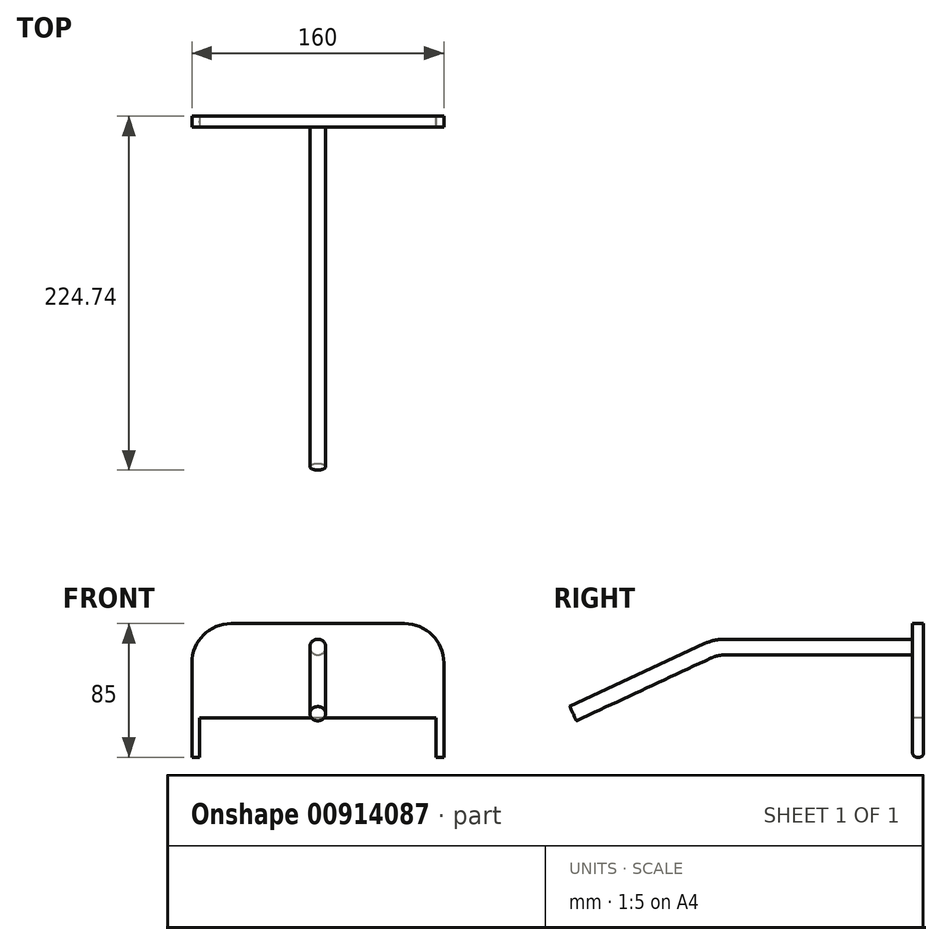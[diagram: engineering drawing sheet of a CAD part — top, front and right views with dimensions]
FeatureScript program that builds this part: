
annotation { "Feature Type Name" : "Feature", "Feature Type Description" : "" }
export const myFeature = defineFeature(function(context is Context, id is Id, definition is map)
    precondition{}
    {
        {
            var Q0;
            Q0=qCreatedBy(makeId("Right.planeOp"),FACE);
            var sketch = newSketch(context, id + "F0", { "sketchPlane" : qUnion([Q0])});
            skLineSegment(sketch, "E0.bottom", {"start": v(3.5, 30) * mm, "end": v(-3.5, 30) * mm});
            skLineSegment(sketch, "E0.top", {"start": v(3.5, -30) * mm, "end": v(-3.5, -30) * mm});
            skLineSegment(sketch, "E0.left", {"start": v(3.5, 30) * mm, "end": v(3.5, -30) * mm});
            skLineSegment(sketch, "E0.right", {"start": v(-3.5, 30) * mm, "end": v(-3.5, -30) * mm});
            skPoint(sketch, "E0.middle", {"position": v(0, 0) * mm});
            skSolve(sketch);
        }
        {
            var Q0;
            Q0=makeQuery(id+"F0.imprint","IMPRINT",FACE,{"disambiguationData":[TD([[makeQuery(id+"F0.imprint","IMPRINT",EDGE,{"derivedFrom":sQuery(id+"F0.wireOp",EDGE,"E0.bottom")}),1.0]])]});
            extrude(context, id + "F1", {"entities" : qUnion([Q0]), "depth" : 75 * mm, "offsetDistance" : 25 * mm, "hasSecondDirection" : true, "secondDirectionOppositeDirection" : true, "secondDirectionDepth" : 75 * mm});
        }
        {
            var Q0;
            Q0=makeQuery(id+"F1.opExtrude","CAP_FACE",FACE,{"disambiguationData":[OSD([sQuery(id+"F0.wireOp",EDGE,"E0.bottom"),sQuery(id+"F0.wireOp",EDGE,"E0.top"),sQuery(id+"F0.wireOp",EDGE,"E0.left"),sQuery(id+"F0.wireOp",EDGE,"E0.right")])],"isStart":false});
            var sketch = newSketch(context, id + "F2", { "sketchPlane" : qUnion([Q0])});
            skLineSegment(sketch, "E1", {"start": v(-3.5, 30) * mm, "end": v(-3.5, -55) * mm});
            skLineSegment(sketch, "E2", {"start": v(-3.5, -55) * mm, "end": v(3.5, -55) * mm});
            skLineSegment(sketch, "E3", {"start": v(3.5, -55) * mm, "end": v(3.5, 30) * mm});
            skLineSegment(sketch, "E4", {"start": v(3.5, 30) * mm, "end": v(-3.5, 30) * mm});
            skSolve(sketch);
        }
        {
            var Q0;
            Q0=qSketchRegion(id+"F2",true);
            extrude(context, id + "F3", {"entities" : qUnion([Q0]), "operationType" : NewBodyOperationType.ADD, "depth" : 5 * mm, "offsetDistance" : 25 * mm});
        }
        {
            var Q0;
            Q0=makeQuery(id+"F1.opExtrude","SWEPT_BODY",BODY,{"disambiguationData":[OSD([sQuery(id+"F0.wireOp",EDGE,"E0.bottom"),sQuery(id+"F0.wireOp",EDGE,"E0.top"),sQuery(id+"F0.wireOp",EDGE,"E0.left"),sQuery(id+"F0.wireOp",EDGE,"E0.right")])]});
            var Q1;
            Q1=qCreatedBy(makeId("Right.planeOp"),FACE);
            mirror(context, id + "F4", {"operationType" : NewBodyOperationType.ADD, "entities" : qUnion([Q0]), "mirrorPlane" : qUnion([Q1])});
        }
        {
            var Q0;
            Q0=makeQuery(id+"F4.opPattern","COPY",EDGE,{"derivedFrom":makeQuery(id+"F3.opExtrude","CAP_EDGE",EDGE,{"disambiguationData":[OSD([sQuery(id+"F2.wireOp",EDGE,"E4")])],"isStart":false}),"instanceName":"1"});
            var Q1;
            Q1=makeQuery(id+"F3.opExtrude","CAP_EDGE",EDGE,{"disambiguationData":[OSD([sQuery(id+"F2.wireOp",EDGE,"E4")])],"isStart":false});
            fillet(context, id + "F5", {"entities" : qUnion([Q0, Q1]), "radius" : 25 * mm, "tangentPropagation" : true, "allowEdgeOverflow" : false});
        }
        {
            var Q0;
            Q0=makeQuery(id+"F4.opPattern","COPY",EDGE,{"derivedFrom":makeQuery(id+"F3.opExtrude","SWEPT_EDGE",EDGE,{"disambiguationData":[OSD([sQuery(id+"F2.wireOp",EDGE,"E1"),sQuery(id+"F2.wireOp",EDGE,"E2")])]}),"instanceName":"1"});
            var Q1;
            Q1=makeQuery(id+"F3.opExtrude","SWEPT_EDGE",EDGE,{"disambiguationData":[OSD([sQuery(id+"F2.wireOp",EDGE,"E1"),sQuery(id+"F2.wireOp",EDGE,"E2")])]});
            var Q2;
            Q2=makeQuery(id+"F4.opPattern","COPY",EDGE,{"derivedFrom":makeQuery(id+"F3.opExtrude","SWEPT_EDGE",EDGE,{"disambiguationData":[OSD([sQuery(id+"F2.wireOp",EDGE,"E2"),sQuery(id+"F2.wireOp",EDGE,"E3")])]}),"instanceName":"1"});
            var Q3;
            Q3=makeQuery(id+"F3.opExtrude","SWEPT_EDGE",EDGE,{"disambiguationData":[OSD([sQuery(id+"F2.wireOp",EDGE,"E2"),sQuery(id+"F2.wireOp",EDGE,"E3")])]});
            fillet(context, id + "F6", {"entities" : qUnion([Q0, Q1, Q2, Q3]), "radius" : 3 * mm, "tangentPropagation" : true, "allowEdgeOverflow" : false});
        }
        {
            var Q0;
            {var subQ0=makeQuery(id+"F3.boolean.opBoolean","MERGE",FACE,{"derivedFrom":[makeQuery(id+"F1.opExtrude","SWEPT_FACE",FACE,{"disambiguationData":[OSD([sQuery(id+"F0.wireOp",EDGE,"E0.right")])]}),makeQuery(id+"F3.opExtrude","SWEPT_FACE",FACE,{"disambiguationData":[OSD([sQuery(id+"F2.wireOp",EDGE,"E1")])]})]});Q0=makeQuery(id+"F4.boolean.opBoolean","MERGE",FACE,{"derivedFrom":[subQ0,makeQuery(id+"F4.opPattern","COPY",FACE,{"derivedFrom":subQ0,"instanceName":"1"})]});}
            var sketch = newSketch(context, id + "F7", { "sketchPlane" : qUnion([Q0])});
            skCircle(sketch, "E5", {"center": v(0, 15) * mm, "radius": 5 * mm});
            skSolve(sketch);
        }
        {
            var Q0;
            Q0=qCreatedBy(makeId("Right.planeOp"),FACE);
            var sketch = newSketch(context, id + "F8", { "sketchPlane" : qUnion([Q0])});
            skLineSegment(sketch, "E6", {"start": v(-3.5, 15) * mm, "end": v(-122.96, 15) * mm});
            skLineSegment(sketch, "E7", {"start": v(-133.52, 12.66) * mm, "end": v(-219.13, -27.26) * mm});
            skPoint(sketch, "E8.visualSharp", {"position": v(-128.5, 15) * mm});
            skArc(sketch, "E8.filletArc", {"start": v(-122.96, 15) * mm, "mid": v(-128.37, 14.4) * mm, "end": v(-133.52, 12.66) * mm});
            skSolve(sketch);
        }
        {
            var Q0;
            Q0=makeQuery(id+"F7.imprint","IMPRINT",FACE,{"disambiguationData":[TD([[makeQuery(id+"F7.imprint","IMPRINT",EDGE,{"derivedFrom":sQuery(id+"F7.wireOp",EDGE,"E5")}),1.0]])]});
            var Q1;
            Q1=sQuery(id+"F7.wireOp",EDGE,"E5");
            var Q2;
            Q2=sQuery(id+"F8.wireOp",EDGE,"E6");
            var Q3;
            Q3=sQuery(id+"F8.wireOp",EDGE,"E8.filletArc");
            var Q4;
            Q4=sQuery(id+"F8.wireOp",EDGE,"E7");
            sweep(context, id + "F9", {"profiles" : qUnion([Q0]), "surfaceProfiles" : qUnion([Q1]), "path" : qUnion([Q2, Q3, Q4])});
        }
    });
